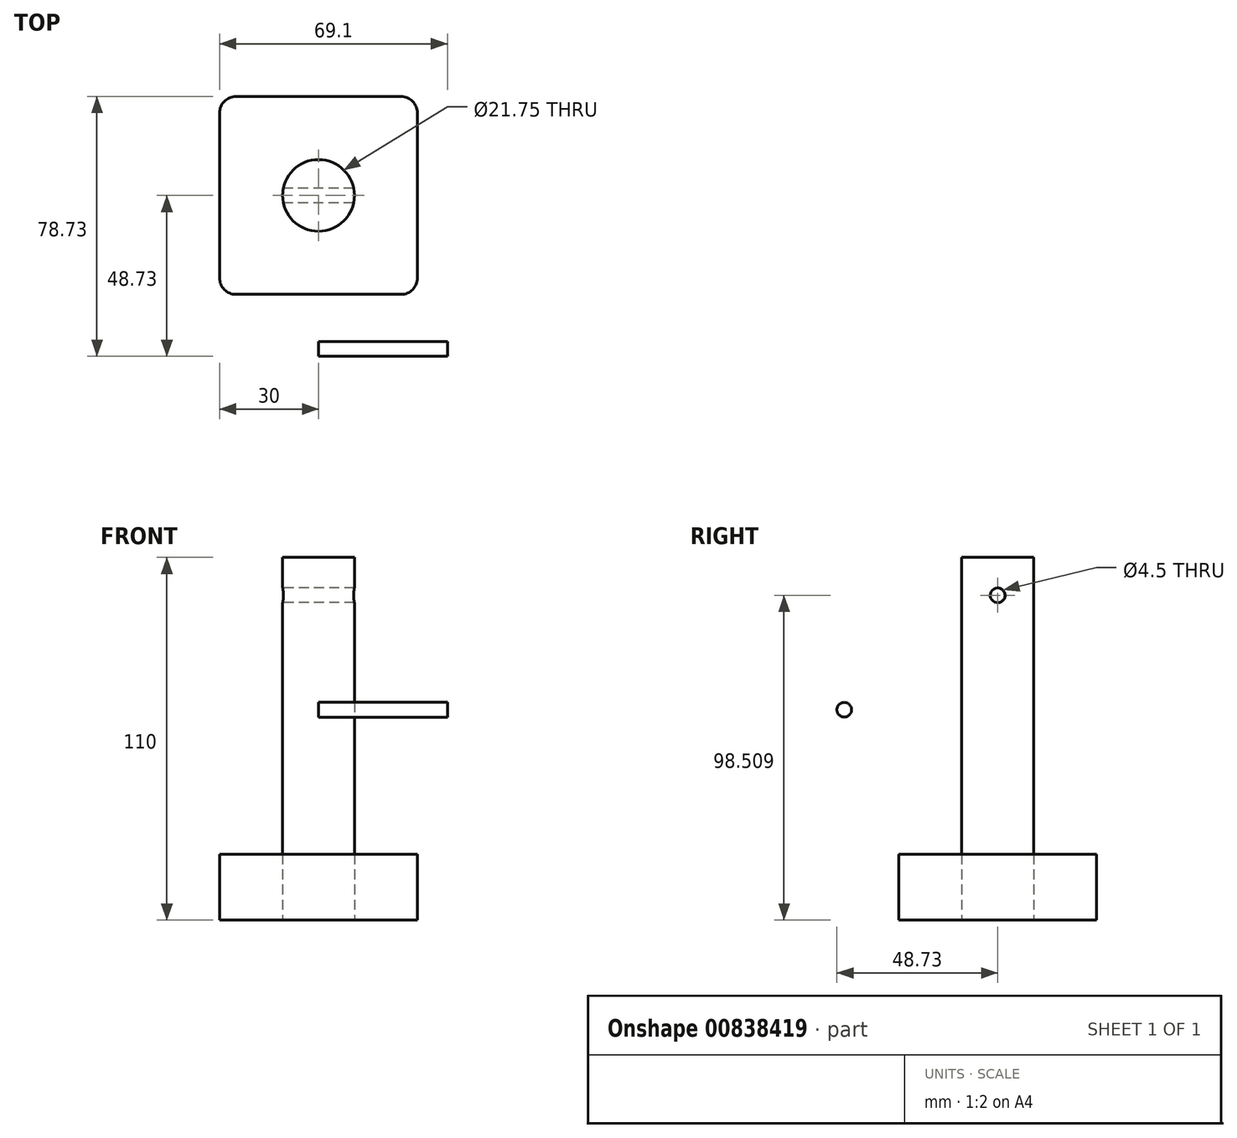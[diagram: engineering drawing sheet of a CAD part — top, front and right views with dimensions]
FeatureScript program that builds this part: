
annotation { "Feature Type Name" : "Feature", "Feature Type Description" : "" }
export const myFeature = defineFeature(function(context is Context, id is Id, definition is map)
    precondition{}
    {
        {
            var Q0;
            Q0=qCreatedBy(makeId("Top.planeOp"),FACE);
            var sketch = newSketch(context, id + "F0", { "sketchPlane" : qUnion([Q0])});
            skCircle(sketch, "E0", {"center": v(0, 0) * mm, "radius": 10.87 * mm});
            skLineSegment(sketch, "E1.bottom", {"start": v(-25, 30) * mm, "end": v(25, 30) * mm});
            skLineSegment(sketch, "E1.top", {"start": v(-25, -30) * mm, "end": v(25, -30) * mm});
            skLineSegment(sketch, "E1.left", {"start": v(-30, 25) * mm, "end": v(-30, -25) * mm});
            skLineSegment(sketch, "E1.right", {"start": v(30, 25) * mm, "end": v(30, -25) * mm});
            skPoint(sketch, "E2.visualSharp", {"position": v(-30, 30) * mm});
            skArc(sketch, "E2.filletArc", {"start": v(-25, 30) * mm, "mid": v(-28.54, 28.54) * mm, "end": v(-30, 25) * mm});
            skPoint(sketch, "E3.visualSharp", {"position": v(30, -30) * mm});
            skArc(sketch, "E3.filletArc", {"start": v(25, -30) * mm, "mid": v(28.54, -28.54) * mm, "end": v(30, -25) * mm});
            skPoint(sketch, "E4.visualSharp", {"position": v(-30, -30) * mm});
            skArc(sketch, "E4.filletArc", {"start": v(-30, -25) * mm, "mid": v(-28.54, -28.54) * mm, "end": v(-25, -30) * mm});
            skPoint(sketch, "E5.visualSharp", {"position": v(30, 30) * mm});
            skArc(sketch, "E5.filletArc", {"start": v(30, 25) * mm, "mid": v(28.54, 28.54) * mm, "end": v(25, 30) * mm});
            skSolve(sketch);
        }
        {
            var Q0;
            Q0=makeQuery(id+"F0.imprint","IMPRINT",FACE,{"disambiguationData":[TD([[makeQuery(id+"F0.imprint","IMPRINT",EDGE,{"derivedFrom":sQuery(id+"F0.wireOp",EDGE,"E0")}),-1.0]])]});
            extrude(context, id + "F1", {"entities" : qUnion([Q0]), "depth" : 20 * mm, "offsetDistance" : 25 * mm});
        }
        {
            var Q0;
            Q0=makeQuery(id+"F1.opExtrude","CAP_FACE",FACE,{"disambiguationData":[OSD([sQuery(id+"F0.wireOp",EDGE,"E0"),sQuery(id+"F0.wireOp",EDGE,"E1.bottom"),sQuery(id+"F0.wireOp",EDGE,"E1.top"),sQuery(id+"F0.wireOp",EDGE,"E1.left"),sQuery(id+"F0.wireOp",EDGE,"E1.right"),sQuery(id+"F0.wireOp",EDGE,"E2.filletArc"),sQuery(id+"F0.wireOp",EDGE,"E3.filletArc"),sQuery(id+"F0.wireOp",EDGE,"E4.filletArc"),sQuery(id+"F0.wireOp",EDGE,"E5.filletArc")])],"isStart":false});
            var sketch = newSketch(context, id + "F2", { "sketchPlane" : qUnion([Q0])});
            skSolve(sketch);
        }
        {
            var Q0;
            Q0=makeQuery(id+"F2.imprint","IMPRINT",FACE,{"disambiguationData":[TD([[makeQuery(id+"F2.imprint","IMPRINT",EDGE,{"derivedFrom":makeQuery(id+"F1.opExtrude","CAP_EDGE",EDGE,{"disambiguationData":[OSD([sQuery(id+"F0.wireOp",EDGE,"E0")])],"isStart":false})}),1.0]])]});
            extrude(context, id + "F3", {"entities" : qUnion([Q0]), "depth" : 90 * mm, "offsetDistance" : 25 * mm});
        }
        {
            var Q0;
            Q0=qCreatedBy(makeId("Right.planeOp"),FACE);
            var sketch = newSketch(context, id + "F4", { "sketchPlane" : qUnion([Q0])});
            skCircle(sketch, "E6", {"center": v(0, 98.5) * mm, "radius": 2.25 * mm});
            skSolve(sketch);
        }
        {
            var Q0;
            Q0 = qSketchRegion(id + "F4", true);
            extrude(context, id + "F5", {"entities" : qUnion([Q0]), "operationType" : NewBodyOperationType.REMOVE, "endBound" : BoundingType.SYMMETRIC, "depth" : 45.4 * mm, "offsetDistance" : 25 * mm});
        }
        {
            var Q0;
            Q0=qCreatedBy(makeId("Right.planeOp"),FACE);
            var sketch = newSketch(context, id + "F6", { "sketchPlane" : qUnion([Q0])});
            skCircle(sketch, "E7", {"center": v(-46.5, 63.8) * mm, "radius": 2.23 * mm});
            skSolve(sketch);
        }
        {
            var Q0;
            Q0=makeQuery(id+"F6.imprint","IMPRINT",FACE,{"disambiguationData":[TD([[makeQuery(id+"F6.imprint","IMPRINT",EDGE,{"derivedFrom":sQuery(id+"F6.wireOp",EDGE,"E7")}),1.0]])]});
            extrude(context, id + "F7", {"entities" : qUnion([Q0]), "depth" : 39.1 * mm, "offsetDistance" : 25 * mm});
        }
    });
